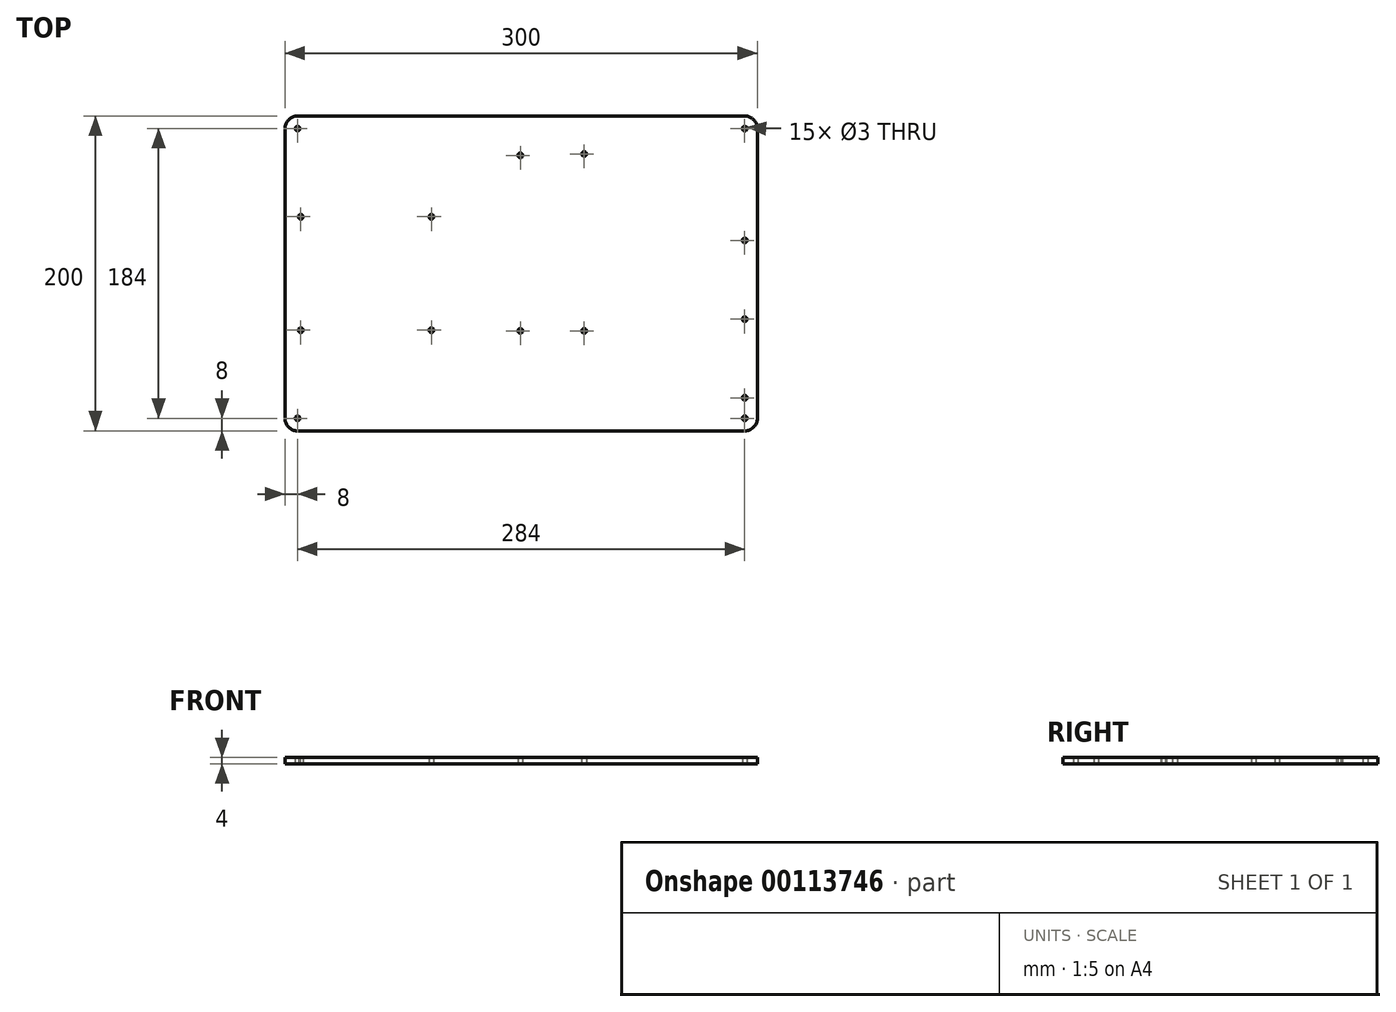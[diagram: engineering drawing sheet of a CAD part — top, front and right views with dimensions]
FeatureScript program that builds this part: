
annotation { "Feature Type Name" : "Feature", "Feature Type Description" : "" }
export const myFeature = defineFeature(function(context is Context, id is Id, definition is map)
    precondition{}
    {
        {
            var Q0;
            Q0=qCreatedBy(makeId("Top.planeOp"),FACE);
            var sketch = newSketch(context, id + "F0", { "sketchPlane" : qUnion([Q0])});
            skLineSegment(sketch, "E0.bottom", {"start": v(142, -100) * mm, "end": v(-142, -100) * mm});
            skLineSegment(sketch, "E0.top", {"start": v(142, 100) * mm, "end": v(-142, 100) * mm});
            skLineSegment(sketch, "E0.left", {"start": v(150, -92) * mm, "end": v(150, 92) * mm});
            skLineSegment(sketch, "E0.right", {"start": v(-150, -92) * mm, "end": v(-150, 92) * mm});
            skPoint(sketch, "E0.middle", {"position": v(0, 0) * mm});
            skPoint(sketch, "E1.visualSharp", {"position": v(-150, 100) * mm});
            skArc(sketch, "E1.filletArc", {"start": v(-142, 100) * mm, "mid": v(-147.66, 97.66) * mm, "end": v(-150, 92) * mm});
            skPoint(sketch, "E2.visualSharp", {"position": v(-150, -100) * mm});
            skArc(sketch, "E2.filletArc", {"start": v(-150, -92) * mm, "mid": v(-147.66, -97.66) * mm, "end": v(-142, -100) * mm});
            skPoint(sketch, "E3.visualSharp", {"position": v(150, -100) * mm});
            skArc(sketch, "E3.filletArc", {"start": v(142, -100) * mm, "mid": v(147.66, -97.66) * mm, "end": v(150, -92) * mm});
            skCircle(sketch, "E4", {"center": v(-142, 92) * mm, "radius": 1.5 * mm});
            skCircle(sketch, "E5", {"center": v(-142, -92) * mm, "radius": 1.5 * mm});
            skCircle(sketch, "E6", {"center": v(142, -92) * mm, "radius": 1.5 * mm});
            skPoint(sketch, "E7.visualSharp", {"position": v(150, 100) * mm});
            skArc(sketch, "E7.filletArc", {"start": v(150, 92) * mm, "mid": v(147.66, 97.66) * mm, "end": v(142, 100) * mm});
            skCircle(sketch, "E8", {"center": v(142, 92) * mm, "radius": 1.5 * mm});
            skLineSegment(sketch, "E9.bottom", {"start": v(-0.5, 75) * mm, "end": v(40, 75) * mm, "construction": true});
            skLineSegment(sketch, "E9.top", {"start": v(-0.5, -36.5) * mm, "end": v(40, -36.5) * mm, "construction": true});
            skLineSegment(sketch, "E9.left", {"start": v(-0.5, 75) * mm, "end": v(-0.5, -36.5) * mm, "construction": true});
            skLineSegment(sketch, "E9.right", {"start": v(40, 75) * mm, "end": v(40, -36.5) * mm, "construction": true});
            skLineSegment(sketch, "E10.bottom", {"start": v(-140, 36) * mm, "end": v(-57, 36) * mm, "construction": true});
            skLineSegment(sketch, "E10.top", {"start": v(-140, -36) * mm, "end": v(-57, -36) * mm, "construction": true});
            skLineSegment(sketch, "E10.left", {"start": v(-140, 36) * mm, "end": v(-140, -36) * mm, "construction": true});
            skLineSegment(sketch, "E10.right", {"start": v(-57, 36) * mm, "end": v(-57, -36) * mm, "construction": true});
            skLineSegment(sketch, "E11", {"start": v(-150, 0) * mm, "end": v(150, 0) * mm, "construction": true});
            skCircle(sketch, "E12", {"center": v(-140, 36) * mm, "radius": 1.5 * mm});
            skCircle(sketch, "E13", {"center": v(-57, 36) * mm, "radius": 1.5 * mm});
            skCircle(sketch, "E14", {"center": v(-57, -36) * mm, "radius": 1.5 * mm});
            skCircle(sketch, "E15", {"center": v(-140, -36) * mm, "radius": 1.5 * mm});
            skCircle(sketch, "E16", {"center": v(-0.5, -36.5) * mm, "radius": 1.5 * mm});
            skCircle(sketch, "E17", {"center": v(40, -36.5) * mm, "radius": 1.5 * mm});
            skCircle(sketch, "E18", {"center": v(-0.5, 75) * mm, "radius": 1.5 * mm});
            skLineSegment(sketch, "E19", {"start": v(142, 92) * mm, "end": v(142, -92) * mm, "construction": true});
            skCircle(sketch, "E20", {"center": v(142, -79) * mm, "radius": 1.5 * mm});
            skCircle(sketch, "E21.0.1.0", {"center": v(142, -29) * mm, "radius": 1.5 * mm});
            skCircle(sketch, "E21.0.2.0", {"center": v(142, 21) * mm, "radius": 1.5 * mm});
            skLineSegment(sketch, "E21.direction1", {"start": v(142, -79) * mm, "end": v(170, -79) * mm, "construction": true});
            skLineSegment(sketch, "E21.direction2", {"start": v(142, -79) * mm, "end": v(142, -29) * mm, "construction": true});
            skCircle(sketch, "E22", {"center": v(40, 75.9) * mm, "radius": 1.5 * mm});
            skSolve(sketch);
        }
        {
            var Q0;
            Q0=makeQuery(id+"F0.imprint","IMPRINT",FACE,{"disambiguationData":[TD([[makeQuery(id+"F0.imprint","IMPRINT",EDGE,{"derivedFrom":sQuery(id+"F0.wireOp",EDGE,"E0.bottom")}),-1.0]])]});
            extrude(context, id + "F1", {"entities" : qUnion([Q0]), "depth" : 4 * mm});
        }
    });
